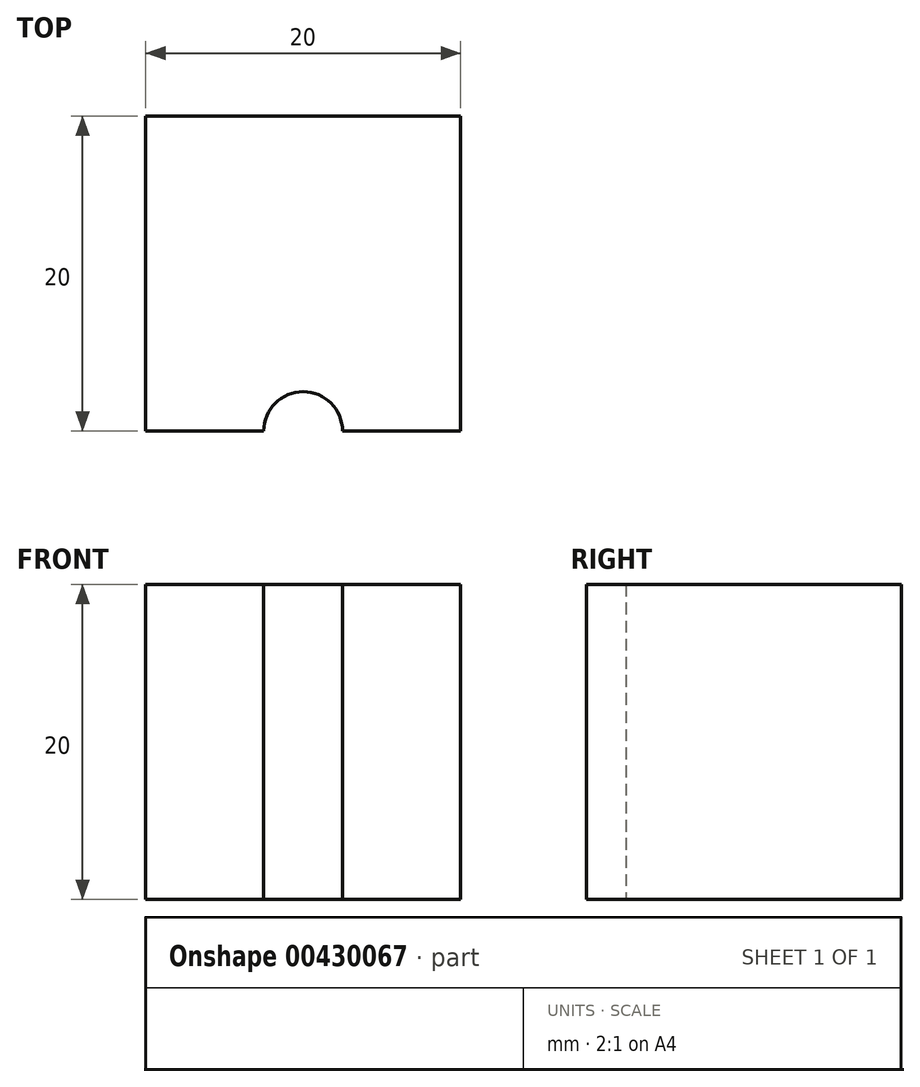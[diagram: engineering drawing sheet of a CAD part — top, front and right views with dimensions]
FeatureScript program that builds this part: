
annotation { "Feature Type Name" : "Feature", "Feature Type Description" : "" }
export const myFeature = defineFeature(function(context is Context, id is Id, definition is map)
    precondition{}
    {
        {
            var Q0;
            Q0=qCreatedBy(makeId("Front.planeOp"),FACE);
            var sketch = newSketch(context, id + "F0", { "sketchPlane" : qUnion([Q0])});
            skLineSegment(sketch, "E0.bottom", {"start": v(10, 10) * mm, "end": v(-10, 10) * mm});
            skLineSegment(sketch, "E0.top", {"start": v(10, -10) * mm, "end": v(-10, -10) * mm});
            skLineSegment(sketch, "E0.left", {"start": v(10, 10) * mm, "end": v(10, -10) * mm});
            skLineSegment(sketch, "E0.right", {"start": v(-10, 10) * mm, "end": v(-10, -10) * mm});
            skPoint(sketch, "E0.middle", {"position": v(0, 0) * mm});
            skSolve(sketch);
        }
        {
            var Q0;
            Q0=makeQuery(id+"F0.imprint","IMPRINT",FACE,{"disambiguationData":[TD([[makeQuery(id+"F0.imprint","IMPRINT",EDGE,{"derivedFrom":sQuery(id+"F0.wireOp",EDGE,"E0.bottom")}),1.0]])]});
            var Q1;
            Q1=sQuery(id+"F0.wireOp",EDGE,"E0.right");
            var Q2;
            Q2=sQuery(id+"F0.wireOp",EDGE,"E0.left");
            var Q3;
            Q3=sQuery(id+"F0.wireOp",EDGE,"E0.top");
            var Q4;
            Q4=sQuery(id+"F0.wireOp",EDGE,"E0.bottom");
            extrude(context, id + "F1", {"entities" : qUnion([Q0]), "surfaceEntities" : qUnion([Q1, Q2, Q3, Q4]), "depth" : 20 * mm});
        }
        {
            var Q0;
            Q0=makeQuery(id+"F1.opExtrude","SWEPT_FACE",FACE,{"disambiguationData":[OSD([sQuery(id+"F0.wireOp",EDGE,"E0.top")])]});
            var sketch = newSketch(context, id + "F2", { "sketchPlane" : qUnion([Q0])});
            skCircle(sketch, "E1", {"center": v(0, 20) * mm, "radius": 2.5 * mm});
            skSolve(sketch);
        }
        {
            var Q0;
            Q0 = qSketchRegion(id + "F2", true);
            extrude(context, id + "F3", {"entities" : qUnion([Q0]), "operationType" : NewBodyOperationType.REMOVE, "oppositeDirection" : true, "depth" : 25 * mm});
        }
    });
